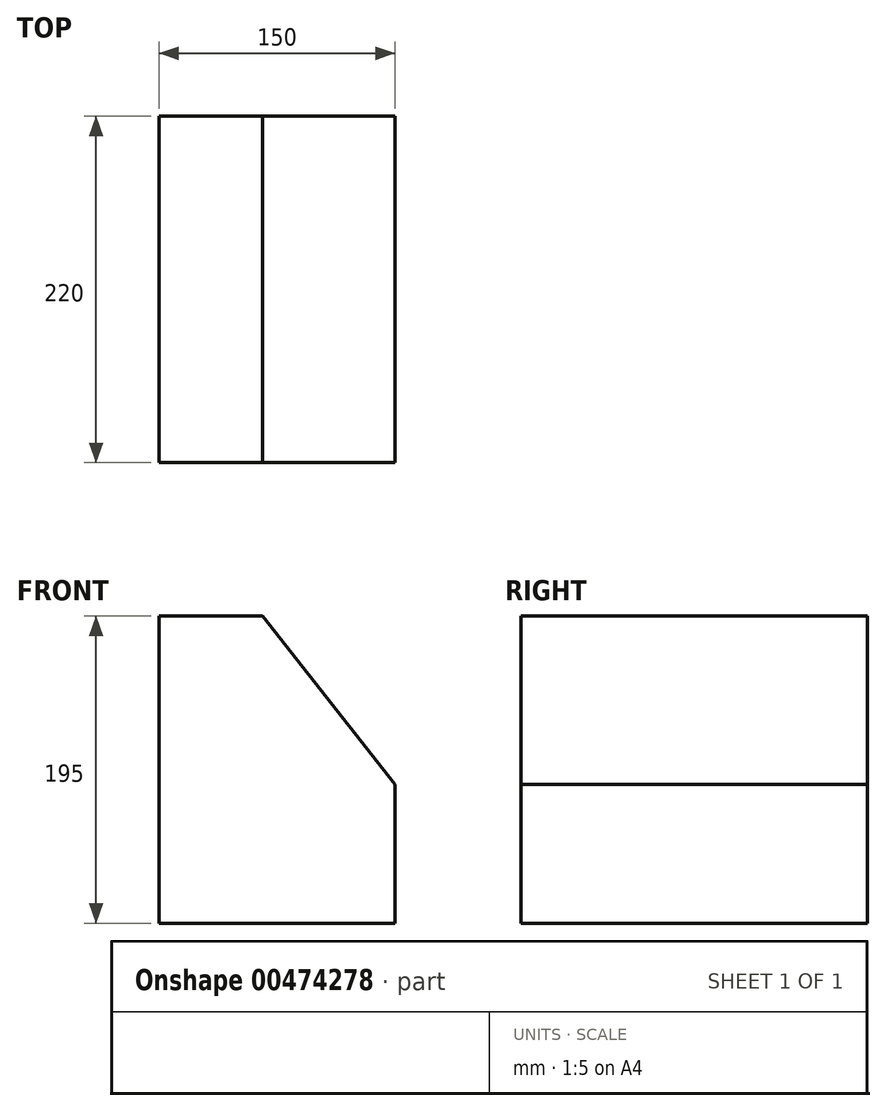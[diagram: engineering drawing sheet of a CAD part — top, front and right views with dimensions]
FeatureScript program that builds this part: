
annotation { "Feature Type Name" : "Feature", "Feature Type Description" : "" }
export const myFeature = defineFeature(function(context is Context, id is Id, definition is map)
    precondition{}
    {
        {
            var Q0;
            Q0=qCreatedBy(makeId("Top.planeOp"),FACE);
            var sketch = newSketch(context, id + "F0", { "sketchPlane" : qUnion([Q0])});
            skLineSegment(sketch, "E0.bottom", {"start": v(-189.55, -150.2) * mm, "end": v(-39.55, -150.2) * mm});
            skLineSegment(sketch, "E0.top", {"start": v(-189.55, 69.8) * mm, "end": v(-39.55, 69.8) * mm});
            skLineSegment(sketch, "E0.left", {"start": v(-189.55, -150.2) * mm, "end": v(-189.55, 69.8) * mm});
            skLineSegment(sketch, "E0.right", {"start": v(-39.55, -150.2) * mm, "end": v(-39.55, 69.8) * mm});
            skSolve(sketch);
        }
        {
            var Q0;
            Q0 = qSketchRegion(id + "F0", true);
            extrude(context, id + "F1", {"entities" : qUnion([Q0]), "depth" : 195 * mm});
        }
        {
            var Q0;
            Q0=makeQuery(id+"F1.opExtrude","SWEPT_FACE",FACE,{"disambiguationData":[OSD([sQuery(id+"F0.wireOp",EDGE,"E0.bottom")])]});
            var sketch = newSketch(context, id + "F2", { "sketchPlane" : qUnion([Q0])});
            skLineSegment(sketch, "E1", {"start": v(-39.55, 195) * mm, "end": v(-39.55, 69.97) * mm});
            skLineSegment(sketch, "E2", {"start": v(-123.8, 195) * mm, "end": v(-39.55, 88.23) * mm});
            skSolve(sketch);
        }
        {
            var Q0;
            {var subQ3=sQuery(id+"F2.wireOp",EDGE,"E2");Q0=makeQuery(id+"F2.imprint","IMPRINT",FACE,{"disambiguationData":[TD([[makeQuery(id+"F2.imprint","IMPRINT",EDGE,{"derivedFrom":subQ3}),1.0]])]});}
            extrude(context, id + "F3", {"entities" : qUnion([Q0]), "operationType" : NewBodyOperationType.REMOVE, "oppositeDirection" : true, "depth" : 220 * mm});
        }
    });
